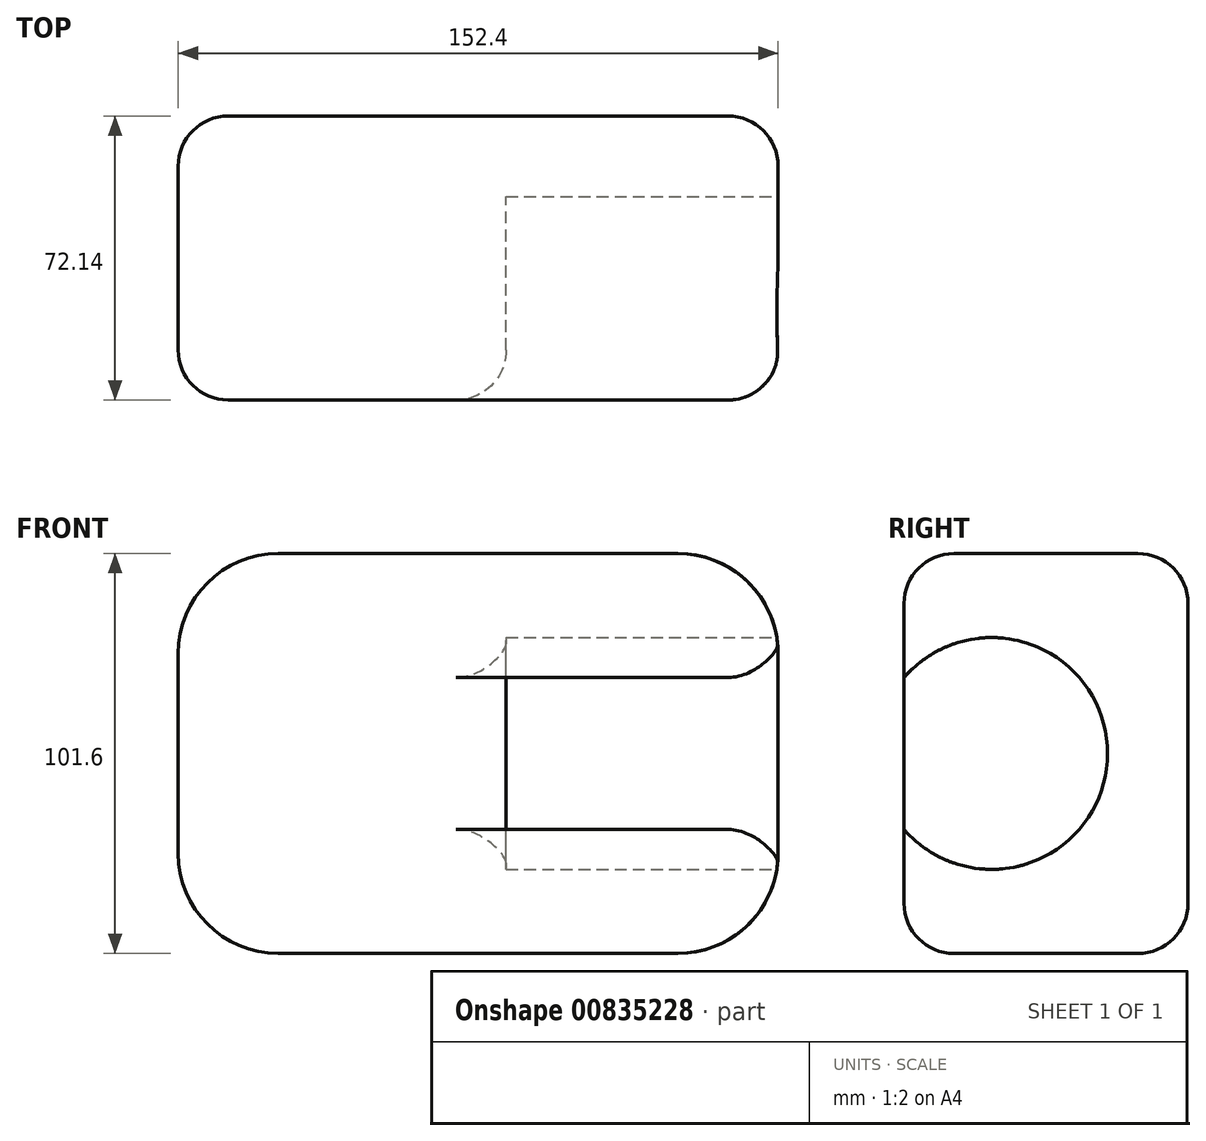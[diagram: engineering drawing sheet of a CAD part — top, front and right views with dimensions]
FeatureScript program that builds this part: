
annotation { "Feature Type Name" : "Feature", "Feature Type Description" : "" }
export const myFeature = defineFeature(function(context is Context, id is Id, definition is map)
    precondition{}
    {
        {
            var Q0;
            Q0=qCreatedBy(makeId("Front.planeOp"),FACE);
            var sketch = newSketch(context, id + "F0", { "sketchPlane" : qUnion([Q0])});
            skLineSegment(sketch, "E0.bottom", {"start": v(76.2, -50.8) * mm, "end": v(-76.2, -50.8) * mm});
            skLineSegment(sketch, "E0.top", {"start": v(76.2, 50.8) * mm, "end": v(-76.2, 50.8) * mm});
            skLineSegment(sketch, "E0.left", {"start": v(76.2, -50.8) * mm, "end": v(76.2, 50.8) * mm});
            skLineSegment(sketch, "E0.right", {"start": v(-76.2, -50.8) * mm, "end": v(-76.2, 50.8) * mm});
            skPoint(sketch, "E0.middle", {"position": v(0, 0) * mm});
            skSolve(sketch);
        }
        {
            var Q0;
            Q0=makeQuery(id+"F0.imprint","IMPRINT",FACE,{"disambiguationData":[TD([[makeQuery(id+"F0.imprint","IMPRINT",EDGE,{"derivedFrom":sQuery(id+"F0.wireOp",EDGE,"E0.bottom")}),-1.0]])]});
            extrude(context, id + "F1", {"entities" : qUnion([Q0]), "depth" : 72.14 * mm, "offsetDistance" : 25.4 * mm});
        }
        {
            var Q0;
            Q0=makeQuery(id+"F1.opExtrude","SWEPT_FACE",FACE,{"disambiguationData":[OSD([sQuery(id+"F0.wireOp",EDGE,"E0.left")])]});
            var sketch = newSketch(context, id + "F2", { "sketchPlane" : qUnion([Q0])});
            skCircle(sketch, "E1", {"center": v(-49.9, 0) * mm, "radius": 29.45 * mm});
            skSolve(sketch);
        }
        {
            var Q0;
            Q0=makeQuery(id+"F2.imprint","IMPRINT",FACE,{"disambiguationData":[TD([[makeQuery(id+"F2.imprint","IMPRINT",EDGE,{"derivedFrom":sQuery(id+"F2.wireOp",EDGE,"E1")}),1.0]])]});
            extrude(context, id + "F3", {"entities" : qUnion([Q0]), "operationType" : NewBodyOperationType.REMOVE, "oppositeDirection" : true, "depth" : 69.1 * mm, "offsetDistance" : 25.4 * mm});
        }
        {
            var Q0;
            Q0=makeQuery(id+"F1.opExtrude","SWEPT_EDGE",EDGE,{"disambiguationData":[OSD([sQuery(id+"F0.wireOp",EDGE,"E0.bottom"),sQuery(id+"F0.wireOp",EDGE,"E0.left")])]});
            var Q1;
            Q1=makeQuery(id+"F1.opExtrude","SWEPT_EDGE",EDGE,{"disambiguationData":[OSD([sQuery(id+"F0.wireOp",EDGE,"E0.bottom"),sQuery(id+"F0.wireOp",EDGE,"E0.right")])]});
            var Q2;
            Q2=makeQuery(id+"F1.opExtrude","SWEPT_EDGE",EDGE,{"disambiguationData":[OSD([sQuery(id+"F0.wireOp",EDGE,"E0.top"),sQuery(id+"F0.wireOp",EDGE,"E0.left")])]});
            var Q3;
            Q3=makeQuery(id+"F1.opExtrude","SWEPT_EDGE",EDGE,{"disambiguationData":[OSD([sQuery(id+"F0.wireOp",EDGE,"E0.top"),sQuery(id+"F0.wireOp",EDGE,"E0.right")])]});
            fillet(context, id + "F4", {"entities" : qUnion([Q0, Q1, Q2, Q3]), "radius" : 25.4 * mm, "tangentPropagation" : true, "allowEdgeOverflow" : false});
        }
        {
            var Q0;
            Q0=makeQuery(id+"F1.opExtrude","CAP_EDGE",EDGE,{"disambiguationData":[OSD([sQuery(id+"F0.wireOp",EDGE,"E0.top")])],"isStart":false});
            var Q1;
            Q1=makeQuery(id+"F1.opExtrude","CAP_EDGE",EDGE,{"disambiguationData":[OSD([sQuery(id+"F0.wireOp",EDGE,"E0.top")])],"isStart":true});
            var Q2;
            Q2=makeQuery(id+"F3.boolean.opBoolean","INTERSECT",EDGE,{"derivedFrom":[makeQuery(id+"F1.opExtrude","CAP_FACE",FACE,{"disambiguationData":[OSD([sQuery(id+"F0.wireOp",EDGE,"E0.bottom"),sQuery(id+"F0.wireOp",EDGE,"E0.top"),sQuery(id+"F0.wireOp",EDGE,"E0.left"),sQuery(id+"F0.wireOp",EDGE,"E0.right")])],"isStart":false}),makeQuery(id+"F3.opExtrude","CAP_FACE",FACE,{"disambiguationData":[OSD([sQuery(id+"F2.wireOp",EDGE,"E1")])],"isStart":false})]});
            fillet(context, id + "F5", {"entities" : qUnion([Q0, Q1, Q2]), "radius" : 12.7 * mm, "tangentPropagation" : true, "allowEdgeOverflow" : false});
        }
    });
